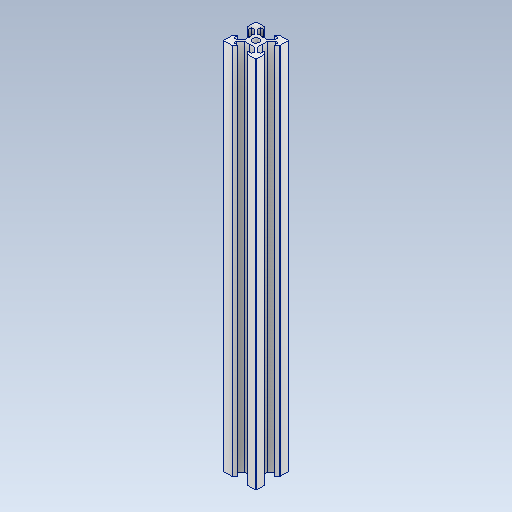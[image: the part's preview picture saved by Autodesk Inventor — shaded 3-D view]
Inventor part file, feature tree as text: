
AUTODESK INVENTOR PART (.ipt)
format: ipt  version: 2021 (Build 250183000, 183)  size: 228,352 bytes
history: native  units: mm
features: sketch x3, extrude x2, fillet x2, other x1, pattern_circular x1, hole x1, projected_geometry x1
ambient origin geometry x8: Origin, YZ Plane, XZ Plane, XY Plane, X Axis, Y Axis, Z Axis, Center Point
bodies: Body1 (feature_tree)
feature tree (11):
  other  "實體1"
  extrude  "擠出1"  Depth=20.0mm
  extrude  "擠出2"  Depth=20.0mm
  fillet  "圓角1"  Radius=230.0mm
  pattern_circular  "環形陣列1"  [2 undecoded]
  hole  "孔1"  [1 undecoded]
  fillet  "圓角2"  Radius=6.2mm
  sketch  "草圖1"
  sketch  "草圖2"
  projected_geometry  "投影迴路1"
  sketch  "草圖3"
note: 3 required parameter values undecoded (feature->parameter linkage not recoverable at this tier; creation-order binding heuristic only, values carry confidence <= 0.55)
